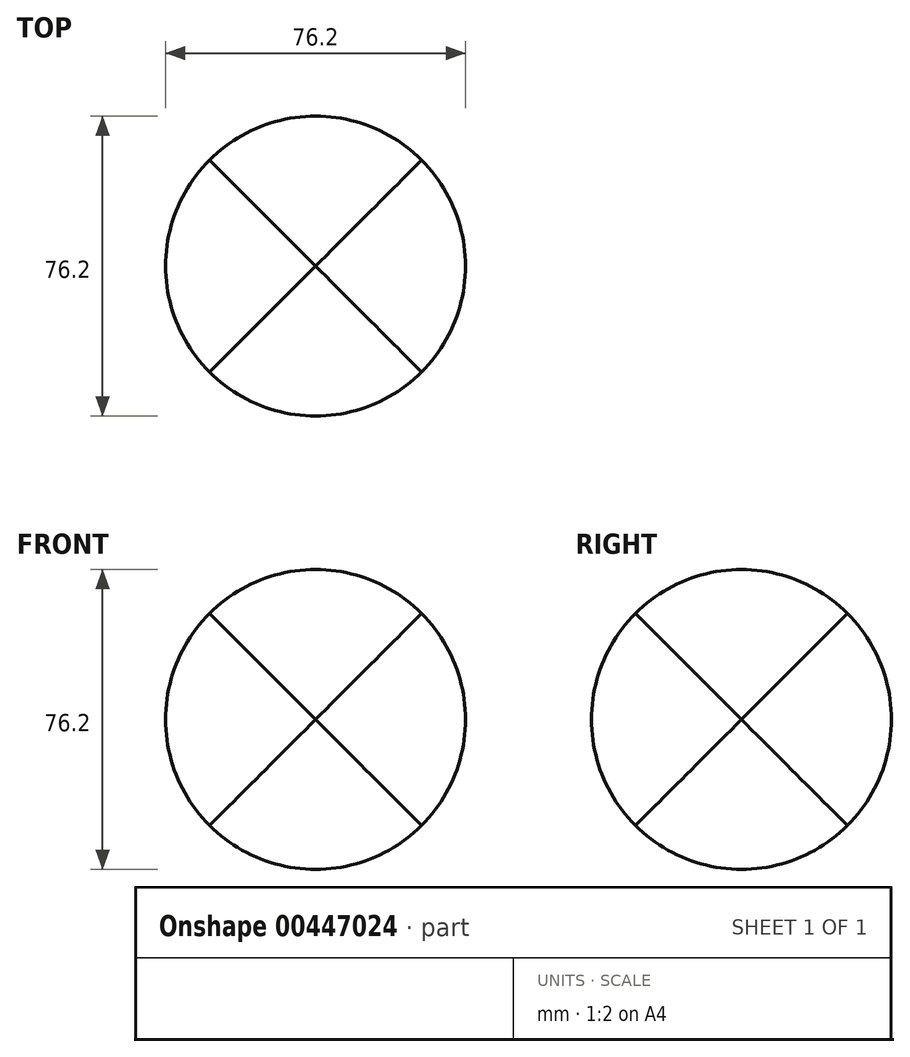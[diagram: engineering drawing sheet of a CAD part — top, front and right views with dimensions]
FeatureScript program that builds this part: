
annotation { "Feature Type Name" : "Feature", "Feature Type Description" : "" }
export const myFeature = defineFeature(function(context is Context, id is Id, definition is map)
    precondition{}
    {
        {
            var Q0;
            Q0=qCreatedBy(makeId("Front.planeOp"),FACE);
            var sketch = newSketch(context, id + "F0", { "sketchPlane" : qUnion([Q0])});
            skLineSegment(sketch, "E0.bottom", {"start": v(0, 0) * mm, "end": v(76.2, 0) * mm});
            skLineSegment(sketch, "E0.top", {"start": v(0, 76.2) * mm, "end": v(76.2, 76.2) * mm});
            skLineSegment(sketch, "E0.left", {"start": v(0, 0) * mm, "end": v(0, 76.2) * mm});
            skLineSegment(sketch, "E0.right", {"start": v(76.2, 0) * mm, "end": v(76.2, 76.2) * mm});
            skSolve(sketch);
        }
        {
            var Q0;
            Q0=qSketchRegion(id+"F0",true);
            extrude(context, id + "F1", {"entities" : qUnion([Q0]), "depth" : 76.2 * mm});
        }
        {
            var Q0;
            Q0=makeQuery(id+"F1.opExtrude","SWEPT_FACE",FACE,{"disambiguationData":[OSD([sQuery(id+"F0.wireOp",EDGE,"E0.top")])]});
            var sketch = newSketch(context, id + "F2", { "sketchPlane" : qUnion([Q0])});
            skLineSegment(sketch, "E1", {"start": v(76.2, -38.1) * mm, "end": v(0, -38.1) * mm, "construction": true});
            skLineSegment(sketch, "E2", {"start": v(38.1, -76.2) * mm, "end": v(38.1, -38.1) * mm, "construction": true});
            skCircle(sketch, "E3", {"center": v(38.1, -38.1) * mm, "radius": 38.1 * mm});
            skSolve(sketch);
        }
        {
            var Q0;
            Q0=makeQuery(id+"F1.opExtrude","CAP_FACE",FACE,{"disambiguationData":[OSD([sQuery(id+"F0.wireOp",EDGE,"E0.bottom"),sQuery(id+"F0.wireOp",EDGE,"E0.top"),sQuery(id+"F0.wireOp",EDGE,"E0.left"),sQuery(id+"F0.wireOp",EDGE,"E0.right")])],"isStart":false});
            var sketch = newSketch(context, id + "F3", { "sketchPlane" : qUnion([Q0])});
            skLineSegment(sketch, "E4", {"start": v(0, 38.1) * mm, "end": v(76.2, 38.1) * mm, "construction": true});
            skLineSegment(sketch, "E5", {"start": v(38.1, 0) * mm, "end": v(38.1, 38.1) * mm, "construction": true});
            skCircle(sketch, "E6", {"center": v(38.1, 38.1) * mm, "radius": 38.1 * mm});
            skSolve(sketch);
        }
        {
            var Q0;
            Q0=makeQuery(id+"F1.opExtrude","SWEPT_FACE",FACE,{"disambiguationData":[OSD([sQuery(id+"F0.wireOp",EDGE,"E0.right")])]});
            var sketch = newSketch(context, id + "F4", { "sketchPlane" : qUnion([Q0])});
            skLineSegment(sketch, "E7", {"start": v(-38.1, 76.2) * mm, "end": v(-38.1, 0) * mm, "construction": true});
            skLineSegment(sketch, "E8", {"start": v(0, 38.1) * mm, "end": v(-38.1, 38.1) * mm, "construction": true});
            skCircle(sketch, "E9", {"center": v(-38.1, 38.1) * mm, "radius": 38.1 * mm});
            skSolve(sketch);
        }
        {
            var Q0;
            {var subQ0=sQuery(id+"F0.wireOp",EDGE,"E0.top");var subQ1=makeQuery(id+"F1.opExtrude","CAP_EDGE",EDGE,{"disambiguationData":[OSD([subQ0])],"isStart":false});var subQ2=sQuery(id+"F2.wireOp",EDGE,"E3");var subQ3=makeQuery(id+"F2.imprint","INTERSECT",VERTEX,{"derivedFrom":[subQ1,subQ2]});Q0=makeQuery(id+"F2.imprint","IMPRINT",FACE,{"disambiguationData":[TD([[makeQuery(id+"F2.imprint","IMPRINT",EDGE,{"disambiguationData":[TD([[subQ3,-1.0]])],"derivedFrom":subQ2}),-1.0]])]});}
            var Q1;
            {var subQ0=sQuery(id+"F0.wireOp",EDGE,"E0.top");var subQ1=makeQuery(id+"F1.opExtrude","CAP_EDGE",EDGE,{"disambiguationData":[OSD([subQ0])],"isStart":true});var subQ2=sQuery(id+"F2.wireOp",EDGE,"E3");var subQ3=makeQuery(id+"F2.imprint","INTERSECT",VERTEX,{"derivedFrom":[subQ1,subQ2]});Q1=makeQuery(id+"F2.imprint","IMPRINT",FACE,{"disambiguationData":[TD([[makeQuery(id+"F2.imprint","IMPRINT",EDGE,{"disambiguationData":[TD([[subQ3,1.0]])],"derivedFrom":subQ2}),-1.0]])]});}
            var Q2;
            {var subQ0=sQuery(id+"F0.wireOp",EDGE,"E0.top");var subQ1=makeQuery(id+"F1.opExtrude","CAP_EDGE",EDGE,{"disambiguationData":[OSD([subQ0])],"isStart":true});var subQ2=sQuery(id+"F2.wireOp",EDGE,"E3");var subQ3=makeQuery(id+"F2.imprint","INTERSECT",VERTEX,{"derivedFrom":[subQ1,subQ2]});Q2=makeQuery(id+"F2.imprint","IMPRINT",FACE,{"disambiguationData":[TD([[makeQuery(id+"F2.imprint","IMPRINT",EDGE,{"disambiguationData":[TD([[subQ3,-1.0]])],"derivedFrom":subQ2}),-1.0]])]});}
            var Q3;
            {var subQ0=sQuery(id+"F0.wireOp",EDGE,"E0.top");var subQ1=makeQuery(id+"F1.opExtrude","CAP_EDGE",EDGE,{"disambiguationData":[OSD([subQ0])],"isStart":false});var subQ2=sQuery(id+"F2.wireOp",EDGE,"E3");var subQ3=makeQuery(id+"F2.imprint","INTERSECT",VERTEX,{"derivedFrom":[subQ1,subQ2]});Q3=makeQuery(id+"F2.imprint","IMPRINT",FACE,{"disambiguationData":[TD([[makeQuery(id+"F2.imprint","IMPRINT",EDGE,{"disambiguationData":[TD([[subQ3,1.0]])],"derivedFrom":subQ2}),-1.0]])]});}
            extrude(context, id + "F5", {"entities" : qUnion([Q0, Q1, Q2, Q3]), "operationType" : NewBodyOperationType.REMOVE, "endBound" : BoundingType.THROUGH_ALL, "oppositeDirection" : true, "depth" : 25.4 * mm});
        }
        {
            var Q0;
            {var subQ1=sQuery(id+"F3.wireOp",EDGE,"E6");var subQ3=makeQuery(id+"F1.opExtrude","CAP_EDGE",EDGE,{"disambiguationData":[OSD([sQuery(id+"F0.wireOp",EDGE,"E0.top")])],"isStart":false});var subQ5=makeQuery(id+"F3.imprint","INTERSECT",VERTEX,{"derivedFrom":[subQ3,subQ1]});Q0=makeQuery(id+"F3.imprint","IMPRINT",FACE,{"disambiguationData":[TD([[makeQuery(id+"F3.imprint","IMPRINT",EDGE,{"disambiguationData":[TD([[subQ5,1.0]])],"derivedFrom":subQ1}),-1.0]])]});}
            var Q1;
            {var subQ1=sQuery(id+"F3.wireOp",EDGE,"E6");var subQ3=makeQuery(id+"F1.opExtrude","CAP_EDGE",EDGE,{"disambiguationData":[OSD([sQuery(id+"F0.wireOp",EDGE,"E0.top")])],"isStart":false});var subQ5=makeQuery(id+"F3.imprint","INTERSECT",VERTEX,{"derivedFrom":[subQ3,subQ1]});Q1=makeQuery(id+"F3.imprint","IMPRINT",FACE,{"disambiguationData":[TD([[makeQuery(id+"F3.imprint","IMPRINT",EDGE,{"disambiguationData":[TD([[subQ5,-1.0]])],"derivedFrom":subQ1}),-1.0]])]});}
            var Q2;
            {var subQ0=makeQuery(id+"F1.opExtrude","CAP_EDGE",EDGE,{"disambiguationData":[OSD([sQuery(id+"F0.wireOp",EDGE,"E0.right")])],"isStart":false});var subQ1=sQuery(id+"F3.wireOp",EDGE,"E6");var subQ2=makeQuery(id+"F3.imprint","INTERSECT",VERTEX,{"derivedFrom":[subQ0,subQ1]});Q2=makeQuery(id+"F3.imprint","IMPRINT",FACE,{"disambiguationData":[TD([[makeQuery(id+"F3.imprint","IMPRINT",EDGE,{"disambiguationData":[TD([[subQ2,1.0]])],"derivedFrom":subQ1}),-1.0]])]});}
            var Q3;
            {var subQ0=makeQuery(id+"F1.opExtrude","CAP_EDGE",EDGE,{"disambiguationData":[OSD([sQuery(id+"F0.wireOp",EDGE,"E0.left")])],"isStart":false});var subQ1=sQuery(id+"F3.wireOp",EDGE,"E6");var subQ2=makeQuery(id+"F3.imprint","INTERSECT",VERTEX,{"derivedFrom":[subQ0,subQ1]});Q3=makeQuery(id+"F3.imprint","IMPRINT",FACE,{"disambiguationData":[TD([[makeQuery(id+"F3.imprint","IMPRINT",EDGE,{"disambiguationData":[TD([[subQ2,-1.0]])],"derivedFrom":subQ1}),-1.0]])]});}
            extrude(context, id + "F6", {"entities" : qUnion([Q0, Q1, Q2, Q3]), "operationType" : NewBodyOperationType.REMOVE, "endBound" : BoundingType.THROUGH_ALL, "oppositeDirection" : true, "depth" : 25.4 * mm});
        }
        {
            var Q0;
            {var subQ0=sQuery(id+"F0.wireOp",EDGE,"E0.right");var subQ1=makeQuery(id+"F1.opExtrude","CAP_EDGE",EDGE,{"disambiguationData":[OSD([subQ0])],"isStart":true});var subQ2=sQuery(id+"F4.wireOp",EDGE,"E9");var subQ3=makeQuery(id+"F4.imprint","INTERSECT",VERTEX,{"derivedFrom":[subQ1,subQ2]});Q0=makeQuery(id+"F4.imprint","IMPRINT",FACE,{"disambiguationData":[TD([[makeQuery(id+"F4.imprint","IMPRINT",EDGE,{"disambiguationData":[TD([[subQ3,-1.0]])],"derivedFrom":subQ2}),-1.0]])]});}
            var Q1;
            {var subQ0=sQuery(id+"F0.wireOp",EDGE,"E0.right");var subQ1=makeQuery(id+"F1.opExtrude","CAP_EDGE",EDGE,{"disambiguationData":[OSD([subQ0])],"isStart":true});var subQ2=sQuery(id+"F4.wireOp",EDGE,"E9");var subQ3=makeQuery(id+"F4.imprint","INTERSECT",VERTEX,{"derivedFrom":[subQ1,subQ2]});Q1=makeQuery(id+"F4.imprint","IMPRINT",FACE,{"disambiguationData":[TD([[makeQuery(id+"F4.imprint","IMPRINT",EDGE,{"disambiguationData":[TD([[subQ3,1.0]])],"derivedFrom":subQ2}),-1.0]])]});}
            var Q2;
            {var subQ0=sQuery(id+"F0.wireOp",EDGE,"E0.right");var subQ1=makeQuery(id+"F1.opExtrude","CAP_EDGE",EDGE,{"disambiguationData":[OSD([subQ0])],"isStart":false});var subQ2=sQuery(id+"F4.wireOp",EDGE,"E9");var subQ3=makeQuery(id+"F4.imprint","INTERSECT",VERTEX,{"derivedFrom":[subQ1,subQ2]});Q2=makeQuery(id+"F4.imprint","IMPRINT",FACE,{"disambiguationData":[TD([[makeQuery(id+"F4.imprint","IMPRINT",EDGE,{"disambiguationData":[TD([[subQ3,-1.0]])],"derivedFrom":subQ2}),-1.0]])]});}
            var Q3;
            {var subQ0=sQuery(id+"F0.wireOp",EDGE,"E0.right");var subQ1=makeQuery(id+"F1.opExtrude","CAP_EDGE",EDGE,{"disambiguationData":[OSD([subQ0])],"isStart":false});var subQ2=sQuery(id+"F4.wireOp",EDGE,"E9");var subQ3=makeQuery(id+"F4.imprint","INTERSECT",VERTEX,{"derivedFrom":[subQ1,subQ2]});Q3=makeQuery(id+"F4.imprint","IMPRINT",FACE,{"disambiguationData":[TD([[makeQuery(id+"F4.imprint","IMPRINT",EDGE,{"disambiguationData":[TD([[subQ3,1.0]])],"derivedFrom":subQ2}),-1.0]])]});}
            extrude(context, id + "F7", {"entities" : qUnion([Q0, Q1, Q2, Q3]), "operationType" : NewBodyOperationType.REMOVE, "endBound" : BoundingType.THROUGH_ALL, "oppositeDirection" : true, "depth" : 25.4 * mm});
        }
    });
